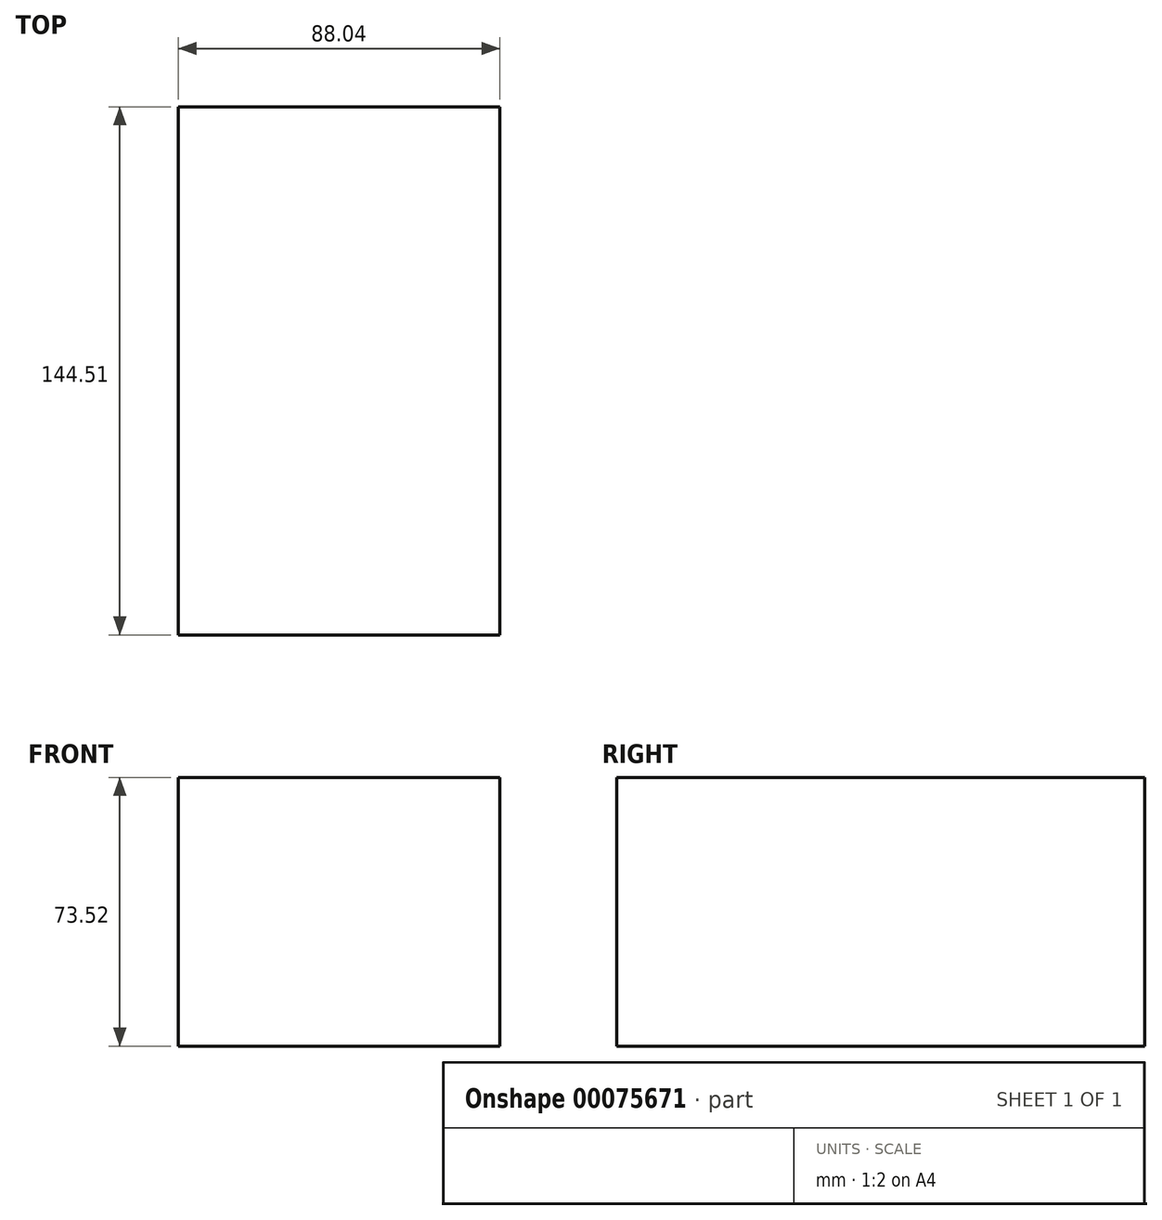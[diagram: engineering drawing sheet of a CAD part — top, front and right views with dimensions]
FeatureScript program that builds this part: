
annotation { "Feature Type Name" : "Feature", "Feature Type Description" : "" }
export const myFeature = defineFeature(function(context is Context, id is Id, definition is map)
    precondition{}
    {
        {
            var Q0;
            Q0=qCreatedBy(makeId("Front.planeOp"),FACE);
            var sketch = newSketch(context, id + "F0", { "sketchPlane" : qUnion([Q0])});
            skLineSegment(sketch, "E0.bottom", {"start": v(-44.02, 36.76) * mm, "end": v(44.02, 36.76) * mm});
            skLineSegment(sketch, "E0.top", {"start": v(-44.02, -36.76) * mm, "end": v(44.02, -36.76) * mm});
            skLineSegment(sketch, "E0.left", {"start": v(-44.02, 36.76) * mm, "end": v(-44.02, -36.76) * mm});
            skLineSegment(sketch, "E0.right", {"start": v(44.02, 36.76) * mm, "end": v(44.02, -36.76) * mm});
            skPoint(sketch, "E0.middle", {"position": v(0, 0) * mm});
            skSolve(sketch);
        }
        {
            var Q0;
            Q0=makeQuery(id+"F0.imprint","IMPRINT",FACE,{"disambiguationData":[TD([[makeQuery(id+"F0.imprint","IMPRINT",EDGE,{"derivedFrom":sQuery(id+"F0.wireOp",EDGE,"E0.bottom")}),-1.0]])]});
            extrude(context, id + "F1", {"entities" : qUnion([Q0]), "depth" : 144.5 * mm});
        }
    });
